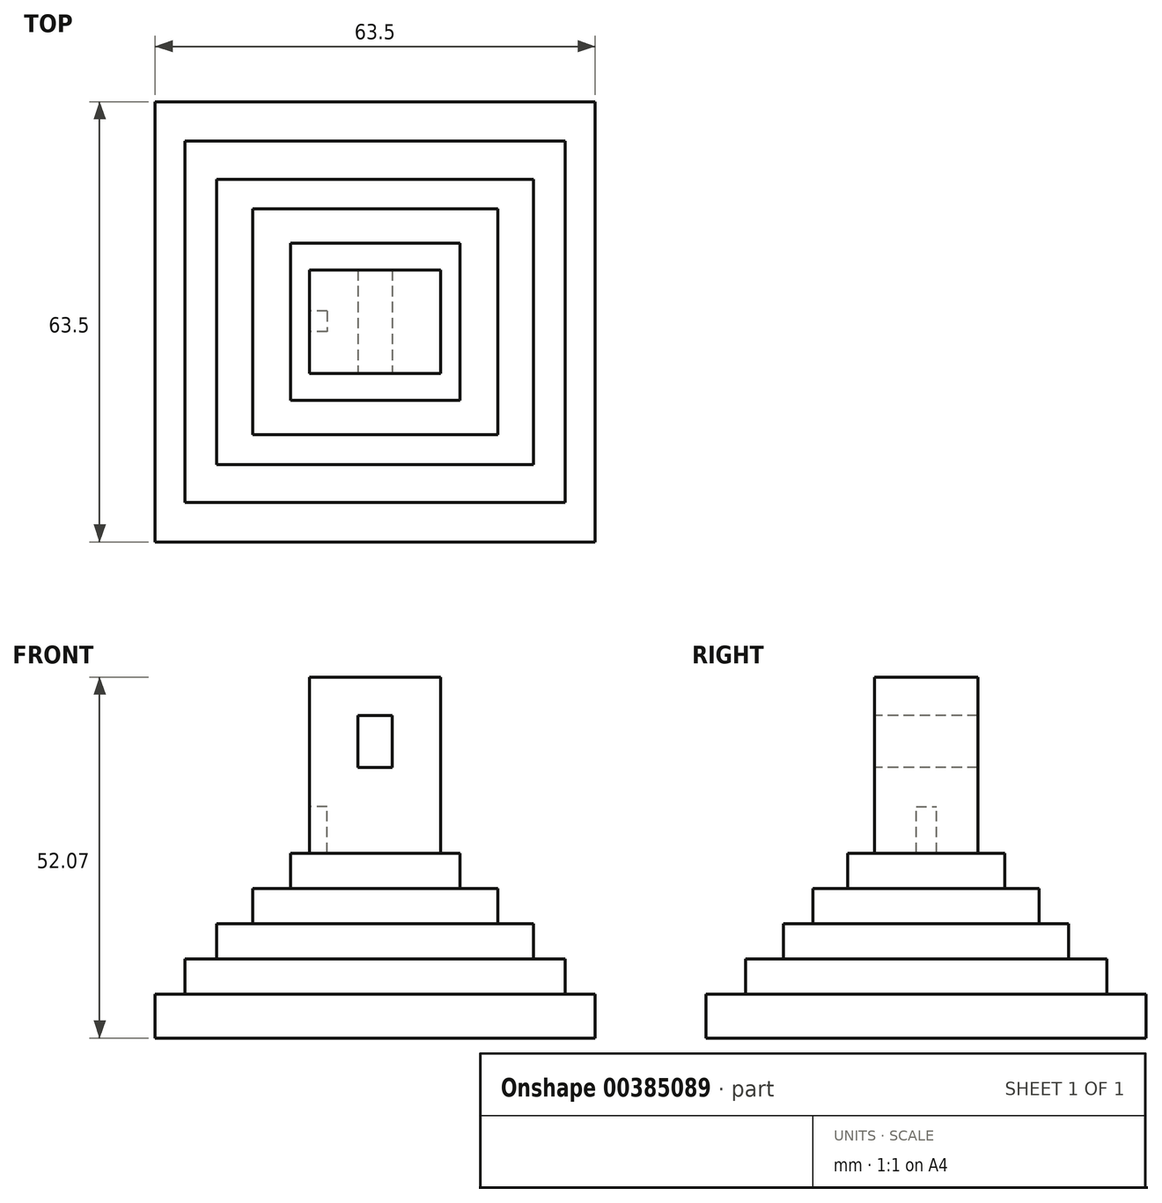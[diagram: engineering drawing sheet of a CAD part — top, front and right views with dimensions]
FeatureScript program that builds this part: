
annotation { "Feature Type Name" : "Feature", "Feature Type Description" : "" }
export const myFeature = defineFeature(function(context is Context, id is Id, definition is map)
    precondition{}
    {
        {
            var Q0;
            Q0=qCreatedBy(makeId("Top.planeOp"),FACE);
            var sketch = newSketch(context, id + "F0", { "sketchPlane" : qUnion([Q0])});
            skLineSegment(sketch, "E0.bottom", {"start": v(31.75, 31.75) * mm, "end": v(-31.75, 31.75) * mm});
            skLineSegment(sketch, "E0.top", {"start": v(31.75, -31.75) * mm, "end": v(-31.75, -31.75) * mm});
            skLineSegment(sketch, "E0.left", {"start": v(31.75, 31.75) * mm, "end": v(31.75, -31.75) * mm});
            skLineSegment(sketch, "E0.right", {"start": v(-31.75, 31.75) * mm, "end": v(-31.75, -31.75) * mm});
            skPoint(sketch, "E0.middle", {"position": v(0, 0) * mm});
            skSolve(sketch);
        }
        {
            var Q0;
            Q0=makeQuery(id+"F0.imprint","IMPRINT",FACE,{"disambiguationData":[TD([[makeQuery(id+"F0.imprint","IMPRINT",EDGE,{"derivedFrom":sQuery(id+"F0.wireOp",EDGE,"E0.bottom")}),1.0]])]});
            extrude(context, id + "F1", {"entities" : qUnion([Q0]), "depth" : 6.35 * mm});
        }
        {
            var Q0;
            Q0=makeQuery(id+"F1.opExtrude","CAP_FACE",FACE,{"disambiguationData":[OSD([sQuery(id+"F0.wireOp",EDGE,"E0.bottom"),sQuery(id+"F0.wireOp",EDGE,"E0.top"),sQuery(id+"F0.wireOp",EDGE,"E0.left"),sQuery(id+"F0.wireOp",EDGE,"E0.right")])],"isStart":false});
            var sketch = newSketch(context, id + "F2", { "sketchPlane" : qUnion([Q0])});
            skLineSegment(sketch, "E1.bottom", {"start": v(27.43, 26.06) * mm, "end": v(-27.43, 26.06) * mm});
            skLineSegment(sketch, "E1.top", {"start": v(27.43, -26.06) * mm, "end": v(-27.43, -26.06) * mm});
            skLineSegment(sketch, "E1.left", {"start": v(27.43, 26.06) * mm, "end": v(27.43, -26.06) * mm});
            skLineSegment(sketch, "E1.right", {"start": v(-27.43, 26.06) * mm, "end": v(-27.43, -26.06) * mm});
            skPoint(sketch, "E1.middle", {"position": v(0, 0) * mm});
            skSolve(sketch);
        }
        {
            var Q0;
            Q0=makeQuery(id+"F2.imprint","IMPRINT",FACE,{"disambiguationData":[TD([[makeQuery(id+"F2.imprint","IMPRINT",EDGE,{"derivedFrom":sQuery(id+"F2.wireOp",EDGE,"E1.bottom")}),1.0]])]});
            extrude(context, id + "F3", {"entities" : qUnion([Q0]), "operationType" : NewBodyOperationType.ADD, "depth" : 5.08 * mm});
        }
        {
            var Q0;
            Q0=makeQuery(id+"F3.opExtrude","CAP_FACE",FACE,{"disambiguationData":[OSD([sQuery(id+"F2.wireOp",EDGE,"E1.bottom"),sQuery(id+"F2.wireOp",EDGE,"E1.top"),sQuery(id+"F2.wireOp",EDGE,"E1.left"),sQuery(id+"F2.wireOp",EDGE,"E1.right")])],"isStart":false});
            var sketch = newSketch(context, id + "F4", { "sketchPlane" : qUnion([Q0])});
            skLineSegment(sketch, "E2.bottom", {"start": v(22.86, 20.57) * mm, "end": v(-22.86, 20.57) * mm});
            skLineSegment(sketch, "E2.top", {"start": v(22.86, -20.57) * mm, "end": v(-22.86, -20.57) * mm});
            skLineSegment(sketch, "E2.left", {"start": v(22.86, 20.57) * mm, "end": v(22.86, -20.57) * mm});
            skLineSegment(sketch, "E2.right", {"start": v(-22.86, 20.57) * mm, "end": v(-22.86, -20.57) * mm});
            skPoint(sketch, "E2.middle", {"position": v(0, 0) * mm});
            skSolve(sketch);
        }
        {
            var Q0;
            Q0=makeQuery(id+"F4.imprint","IMPRINT",FACE,{"disambiguationData":[TD([[makeQuery(id+"F4.imprint","IMPRINT",EDGE,{"derivedFrom":sQuery(id+"F4.wireOp",EDGE,"E2.bottom")}),1.0]])]});
            extrude(context, id + "F5", {"entities" : qUnion([Q0]), "operationType" : NewBodyOperationType.ADD, "depth" : 5.08 * mm});
        }
        {
            var Q0;
            Q0=makeQuery(id+"F5.opExtrude","CAP_FACE",FACE,{"disambiguationData":[OSD([sQuery(id+"F4.wireOp",EDGE,"E2.bottom"),sQuery(id+"F4.wireOp",EDGE,"E2.top"),sQuery(id+"F4.wireOp",EDGE,"E2.left"),sQuery(id+"F4.wireOp",EDGE,"E2.right")])],"isStart":false});
            var sketch = newSketch(context, id + "F6", { "sketchPlane" : qUnion([Q0])});
            skLineSegment(sketch, "E3.bottom", {"start": v(17.68, 16.3) * mm, "end": v(-17.68, 16.3) * mm});
            skLineSegment(sketch, "E3.top", {"start": v(17.68, -16.3) * mm, "end": v(-17.68, -16.3) * mm});
            skLineSegment(sketch, "E3.left", {"start": v(17.68, 16.3) * mm, "end": v(17.68, -16.3) * mm});
            skLineSegment(sketch, "E3.right", {"start": v(-17.68, 16.3) * mm, "end": v(-17.68, -16.3) * mm});
            skPoint(sketch, "E3.middle", {"position": v(0, 0) * mm});
            skSolve(sketch);
        }
        {
            var Q0;
            Q0=makeQuery(id+"F6.imprint","IMPRINT",FACE,{"disambiguationData":[TD([[makeQuery(id+"F6.imprint","IMPRINT",EDGE,{"derivedFrom":sQuery(id+"F6.wireOp",EDGE,"E3.bottom")}),1.0]])]});
            extrude(context, id + "F7", {"entities" : qUnion([Q0]), "operationType" : NewBodyOperationType.ADD, "depth" : 5.08 * mm});
        }
        {
            var Q0;
            Q0=makeQuery(id+"F7.opExtrude","CAP_FACE",FACE,{"disambiguationData":[OSD([sQuery(id+"F6.wireOp",EDGE,"E3.bottom"),sQuery(id+"F6.wireOp",EDGE,"E3.top"),sQuery(id+"F6.wireOp",EDGE,"E3.left"),sQuery(id+"F6.wireOp",EDGE,"E3.right")])],"isStart":false});
            var sketch = newSketch(context, id + "F8", { "sketchPlane" : qUnion([Q0])});
            skLineSegment(sketch, "E4.bottom", {"start": v(12.23, 11.34) * mm, "end": v(-12.23, 11.34) * mm});
            skLineSegment(sketch, "E4.top", {"start": v(12.23, -11.34) * mm, "end": v(-12.23, -11.34) * mm});
            skLineSegment(sketch, "E4.left", {"start": v(12.23, 11.34) * mm, "end": v(12.23, -11.34) * mm});
            skLineSegment(sketch, "E4.right", {"start": v(-12.23, 11.34) * mm, "end": v(-12.23, -11.34) * mm});
            skPoint(sketch, "E4.middle", {"position": v(0, 0) * mm});
            skSolve(sketch);
        }
        {
            var Q0;
            Q0=makeQuery(id+"F8.imprint","IMPRINT",FACE,{"disambiguationData":[TD([[makeQuery(id+"F8.imprint","IMPRINT",EDGE,{"derivedFrom":sQuery(id+"F8.wireOp",EDGE,"E4.bottom")}),1.0]])]});
            extrude(context, id + "F9", {"entities" : qUnion([Q0]), "operationType" : NewBodyOperationType.ADD, "depth" : 5.08 * mm});
        }
        {
            var Q0;
            Q0=makeQuery(id+"F9.opExtrude","CAP_FACE",FACE,{"disambiguationData":[OSD([sQuery(id+"F8.wireOp",EDGE,"E4.bottom"),sQuery(id+"F8.wireOp",EDGE,"E4.top"),sQuery(id+"F8.wireOp",EDGE,"E4.left"),sQuery(id+"F8.wireOp",EDGE,"E4.right")])],"isStart":false});
            var sketch = newSketch(context, id + "F10", { "sketchPlane" : qUnion([Q0])});
            skLineSegment(sketch, "E5.bottom", {"start": v(9.45, 7.47) * mm, "end": v(-9.45, 7.47) * mm});
            skLineSegment(sketch, "E5.top", {"start": v(9.45, -7.47) * mm, "end": v(-9.45, -7.47) * mm});
            skLineSegment(sketch, "E5.left", {"start": v(9.45, 7.47) * mm, "end": v(9.45, -7.47) * mm});
            skLineSegment(sketch, "E5.right", {"start": v(-9.45, 7.47) * mm, "end": v(-9.45, -7.47) * mm});
            skPoint(sketch, "E5.middle", {"position": v(0, 0) * mm});
            skSolve(sketch);
        }
        {
            var Q0;
            Q0 = qSketchRegion(id + "F10", true);
            extrude(context, id + "F11", {"entities" : qUnion([Q0]), "operationType" : NewBodyOperationType.ADD, "depth" : 25.4 * mm});
        }
        {
            var Q0;
            Q0=makeQuery(id+"F11.opExtrude","SWEPT_FACE",FACE,{"disambiguationData":[OSD([sQuery(id+"F10.wireOp",EDGE,"E5.top")])]});
            var sketch = newSketch(context, id + "F12", { "sketchPlane" : qUnion([Q0])});
            skLineSegment(sketch, "E6.bottom", {"start": v(2.48, 39) * mm, "end": v(-2.48, 39) * mm});
            skLineSegment(sketch, "E6.top", {"start": v(2.48, 46.5) * mm, "end": v(-2.48, 46.5) * mm});
            skLineSegment(sketch, "E6.left", {"start": v(2.48, 39) * mm, "end": v(2.48, 46.5) * mm});
            skLineSegment(sketch, "E6.right", {"start": v(-2.48, 39) * mm, "end": v(-2.48, 46.5) * mm});
            skPoint(sketch, "E6.middle", {"position": v(0, 42.75) * mm});
            skSolve(sketch);
        }
        {
            var Q0;
            Q0=makeQuery(id+"F12.imprint","IMPRINT",FACE,{"disambiguationData":[TD([[makeQuery(id+"F12.imprint","IMPRINT",EDGE,{"derivedFrom":sQuery(id+"F12.wireOp",EDGE,"E6.bottom")}),-1.0]])]});
            extrude(context, id + "F13", {"entities" : qUnion([Q0]), "operationType" : NewBodyOperationType.REMOVE, "oppositeDirection" : true, "depth" : 39.37 * mm});
        }
        {
            var Q0;
            Q0=makeQuery(id+"F11.opExtrude","SWEPT_FACE",FACE,{"disambiguationData":[OSD([sQuery(id+"F10.wireOp",EDGE,"E5.right")])]});
            var sketch = newSketch(context, id + "F14", { "sketchPlane" : qUnion([Q0])});
            skLineSegment(sketch, "E7.bottom", {"start": v(1.44, 26.67) * mm, "end": v(-1.53, 26.67) * mm});
            skLineSegment(sketch, "E7.top", {"start": v(1.44, 33.4) * mm, "end": v(-1.53, 33.4) * mm});
            skLineSegment(sketch, "E7.left", {"start": v(1.44, 26.67) * mm, "end": v(1.44, 33.4) * mm});
            skLineSegment(sketch, "E7.right", {"start": v(-1.53, 26.67) * mm, "end": v(-1.53, 33.4) * mm});
            skSolve(sketch);
        }
        {
            var Q0;
            Q0=makeQuery(id+"F14.imprint","IMPRINT",FACE,{"disambiguationData":[TD([[makeQuery(id+"F14.imprint","IMPRINT",EDGE,{"derivedFrom":sQuery(id+"F14.wireOp",EDGE,"E7.bottom")}),1.0]])]});
            extrude(context, id + "F15", {"entities" : qUnion([Q0]), "operationType" : NewBodyOperationType.REMOVE, "oppositeDirection" : true, "depth" : 2.54 * mm});
        }
    });
